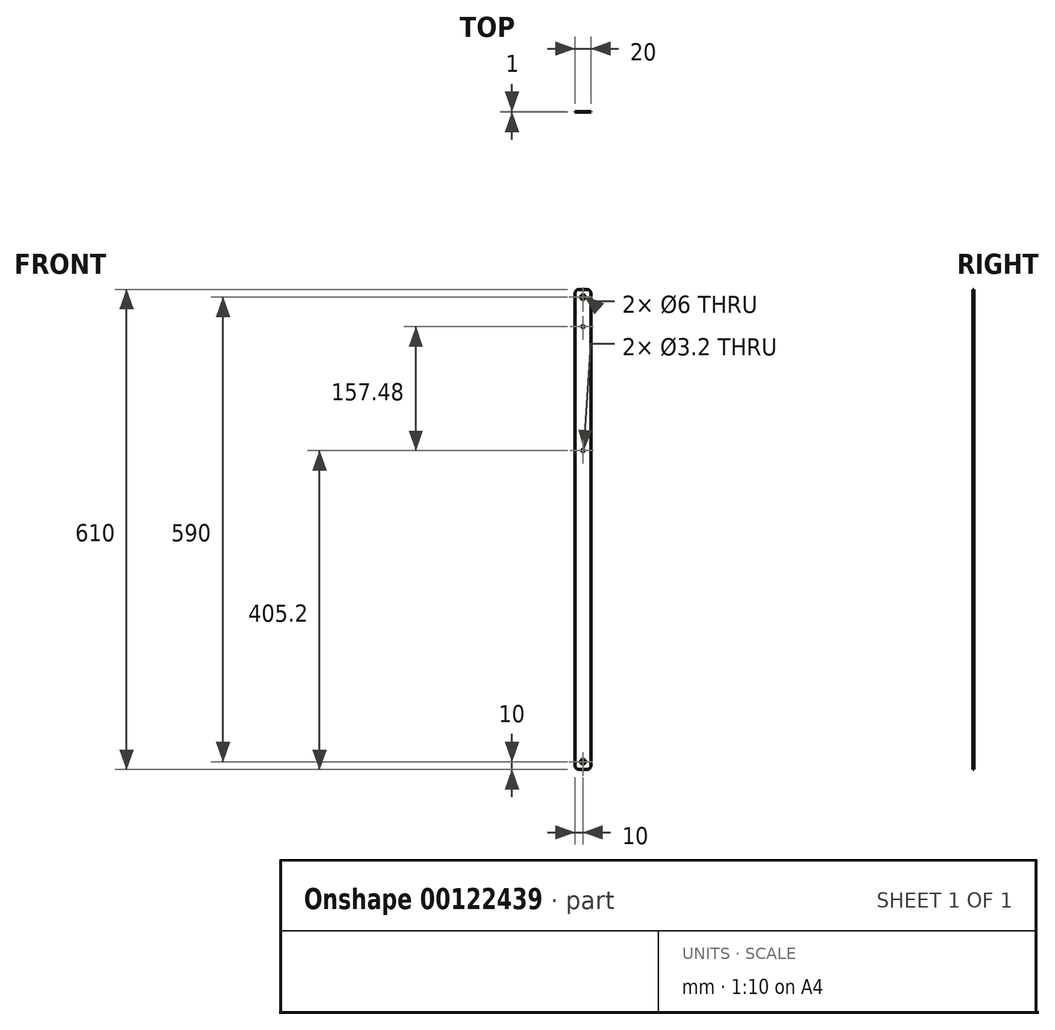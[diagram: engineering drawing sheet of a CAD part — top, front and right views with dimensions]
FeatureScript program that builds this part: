
annotation { "Feature Type Name" : "Feature", "Feature Type Description" : "" }
export const myFeature = defineFeature(function(context is Context, id is Id, definition is map)
    precondition{}
    {
        {
            var Q0;
            Q0=qCreatedBy(makeId("Front.planeOp"),FACE);
            var sketch = newSketch(context, id + "F0", { "sketchPlane" : qUnion([Q0])});
            skLineSegment(sketch, "E0.bottom", {"start": v(5, 0) * mm, "end": v(15, 0) * mm});
            skLineSegment(sketch, "E0.top", {"start": v(5, 610) * mm, "end": v(15, 610) * mm});
            skLineSegment(sketch, "E0.left", {"start": v(0, 5) * mm, "end": v(0, 605) * mm});
            skLineSegment(sketch, "E0.right", {"start": v(20, 5) * mm, "end": v(20, 605) * mm});
            skCircle(sketch, "E1", {"center": v(10, 10) * mm, "radius": 3 * mm});
            skPoint(sketch, "E1.centerSnap0", {"position": v(10, 0) * mm});
            skCircle(sketch, "E2", {"center": v(10, 600) * mm, "radius": 3 * mm});
            skPoint(sketch, "E2.centerSnap0", {"position": v(10, 610) * mm});
            skCircle(sketch, "E3", {"center": v(10, 562.68) * mm, "radius": 1.6 * mm});
            skCircle(sketch, "E4", {"center": v(10, 405.2) * mm, "radius": 1.6 * mm});
            skPoint(sketch, "E5.visualSharp", {"position": v(0, 610) * mm});
            skArc(sketch, "E5.filletArc", {"start": v(5, 610) * mm, "mid": v(1.46, 608.54) * mm, "end": v(0, 605) * mm});
            skPoint(sketch, "E6.visualSharp", {"position": v(20, 610) * mm});
            skArc(sketch, "E6.filletArc", {"start": v(20, 605) * mm, "mid": v(18.54, 608.54) * mm, "end": v(15, 610) * mm});
            skPoint(sketch, "E7.visualSharp", {"position": v(0, 0) * mm});
            skArc(sketch, "E7.filletArc", {"start": v(0, 5) * mm, "mid": v(1.46, 1.46) * mm, "end": v(5, 0) * mm});
            skPoint(sketch, "E8.visualSharp", {"position": v(20, 0) * mm});
            skArc(sketch, "E8.filletArc", {"start": v(15, 0) * mm, "mid": v(18.54, 1.46) * mm, "end": v(20, 5) * mm});
            skSolve(sketch);
        }
        {
            var Q0;
            Q0=qSketchRegion(id+"F0",true);
            extrude(context, id + "F1", {"entities" : qUnion([Q0]), "depth" : 1 * mm});
        }
    });
